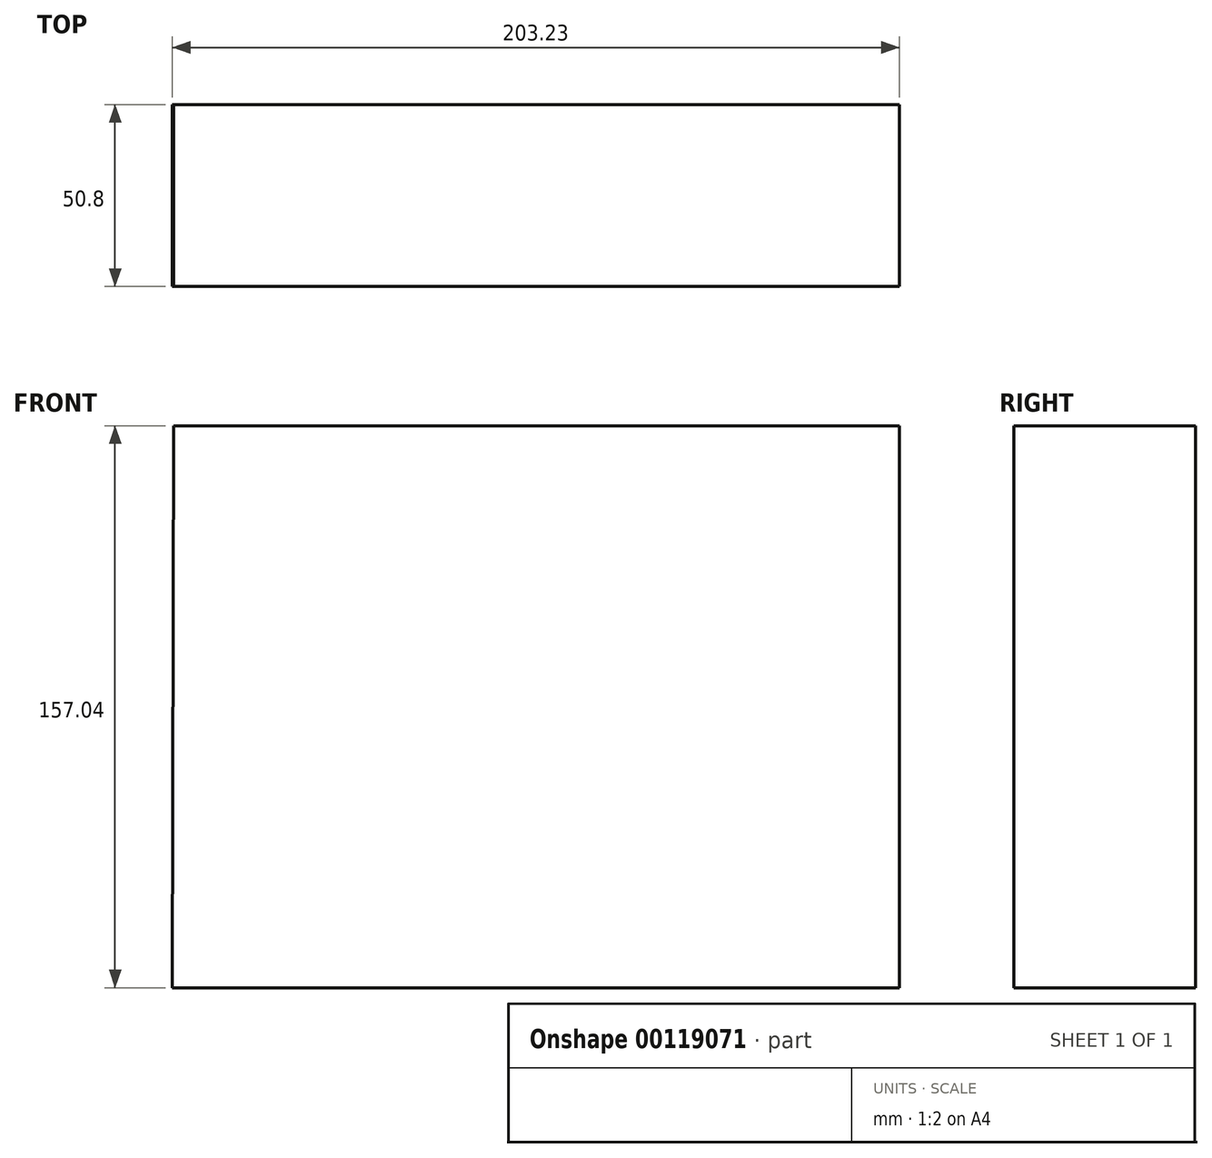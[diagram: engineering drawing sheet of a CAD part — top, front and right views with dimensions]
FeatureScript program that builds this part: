
annotation { "Feature Type Name" : "Feature", "Feature Type Description" : "" }
export const myFeature = defineFeature(function(context is Context, id is Id, definition is map)
    precondition{}
    {
        {
            var Q0;
            Q0=qCreatedBy(makeId("Front.planeOp"),FACE);
            var sketch = newSketch(context, id + "F0", { "sketchPlane" : qUnion([Q0])});
            skCircle(sketch, "E0", {"center": v(0, 0) * mm, "radius": 68.7 * mm});
            skCircle(sketch, "E1", {"center": v(0, 0) * mm, "radius": 25.42 * mm});
            skCircle(sketch, "E2", {"center": v(0, 0) * mm, "radius": 54.89 * mm});
            skLineSegment(sketch, "E3", {"start": v(-41.7, 35.68) * mm, "end": v(-19.6, 16.2) * mm});
            skLineSegment(sketch, "E4", {"start": v(-23.88, 8.7) * mm, "end": v(-46.71, 28.82) * mm});
            skLineSegment(sketch, "E5", {"start": v(-4.77, 54.68) * mm, "end": v(-4.77, 24.97) * mm});
            skLineSegment(sketch, "E6", {"start": v(5.39, 54.62) * mm, "end": v(5.39, 24.84) * mm});
            skLineSegment(sketch, "E7", {"start": v(17.58, 18.36) * mm, "end": v(38.51, 39.11) * mm});
            skLineSegment(sketch, "E8", {"start": v(38.51, 39.11) * mm, "end": v(17.58, 18.36) * mm});
            skLineSegment(sketch, "E9", {"start": v(22.8, 11.24) * mm, "end": v(44.23, 32.5) * mm});
            skLineSegment(sketch, "E10", {"start": v(24.53, -6.66) * mm, "end": v(51.45, -19.11) * mm});
            skLineSegment(sketch, "E11", {"start": v(21.26, -13.93) * mm, "end": v(48.14, -26.36) * mm});
            skLineSegment(sketch, "E12", {"start": v(6.01, -24.7) * mm, "end": v(6.01, -54.56) * mm});
            skLineSegment(sketch, "E13", {"start": v(6.01, -54.56) * mm, "end": v(6.01, -24.7) * mm});
            skLineSegment(sketch, "E14", {"start": v(-4.16, -25.08) * mm, "end": v(-4.16, -54.73) * mm});
            skLineSegment(sketch, "E15", {"start": v(-4.16, -54.73) * mm, "end": v(-4.16, -25.08) * mm});
            skLineSegment(sketch, "E16", {"start": v(-22.39, -12.04) * mm, "end": v(-48.5, -25.7) * mm});
            skLineSegment(sketch, "E17", {"start": v(-48.5, -25.7) * mm, "end": v(-22.39, -12.04) * mm});
            skLineSegment(sketch, "E18", {"start": v(-24.94, -4.9) * mm, "end": v(-51.56, -18.81) * mm});
            skCircle(sketch, "E19", {"center": v(0, 0) * mm, "radius": 21.1 * mm});
            skSolve(sketch);
        }
        {
            var Q0;
            {var subQ0=sQuery(id+"F0.wireOp",EDGE,"E3");Q0=makeQuery(id+"F0.imprint","IMPRINT",FACE,{"disambiguationData":[TD([[makeQuery(id+"F0.imprint","IMPRINT",EDGE,{"derivedFrom":subQ0}),-1.0]])]});}
            var Q1;
            {var subQ0=sQuery(id+"F0.wireOp",EDGE,"E17");Q1=makeQuery(id+"F0.imprint","IMPRINT",FACE,{"disambiguationData":[TD([[makeQuery(id+"F0.imprint","IMPRINT",EDGE,{"derivedFrom":subQ0}),1.0]])]});}
            var Q2;
            Q2=makeQuery(id+"F0.imprint","IMPRINT",FACE,{"disambiguationData":[TD([[makeQuery(id+"F0.imprint","IMPRINT",EDGE,{"derivedFrom":sQuery(id+"F0.wireOp",EDGE,"E0")}),1.0]])]});
            var Q3;
            {var subQ0=sQuery(id+"F0.wireOp",EDGE,"E13");Q3=makeQuery(id+"F0.imprint","IMPRINT",FACE,{"disambiguationData":[TD([[makeQuery(id+"F0.imprint","IMPRINT",EDGE,{"derivedFrom":subQ0}),1.0]])]});}
            var Q4;
            {var subQ0=sQuery(id+"F0.wireOp",EDGE,"E10");Q4=makeQuery(id+"F0.imprint","IMPRINT",FACE,{"disambiguationData":[TD([[makeQuery(id+"F0.imprint","IMPRINT",EDGE,{"derivedFrom":subQ0}),-1.0]])]});}
            var Q5;
            {var subQ0=sQuery(id+"F0.wireOp",EDGE,"E8");Q5=makeQuery(id+"F0.imprint","IMPRINT",FACE,{"disambiguationData":[TD([[makeQuery(id+"F0.imprint","IMPRINT",EDGE,{"derivedFrom":subQ0}),1.0]])]});}
            var Q6;
            {var subQ0=sQuery(id+"F0.wireOp",EDGE,"E5");Q6=makeQuery(id+"F0.imprint","IMPRINT",FACE,{"disambiguationData":[TD([[makeQuery(id+"F0.imprint","IMPRINT",EDGE,{"derivedFrom":subQ0}),1.0]])]});}
            var Q7;
            Q7=makeQuery(id+"F0.imprint","IMPRINT",FACE,{"disambiguationData":[TD([[makeQuery(id+"F0.imprint","IMPRINT",EDGE,{"derivedFrom":sQuery(id+"F0.wireOp",EDGE,"E19")}),-1.0]])]});
            extrude(context, id + "F1", {"entities" : qUnion([Q0, Q1, Q2, Q3, Q4, Q5, Q6, Q7]), "depth" : 25.4 * mm});
        }
        {
            var Q0;
            Q0=makeQuery(id+"F1.opExtrude","SWEPT_FACE",FACE,{"disambiguationData":[OSD([sQuery(id+"F0.wireOp",EDGE,"E0")])]});
            shell(context, id + "F2", {"entities" : qUnion([Q0]), "thickness" : 2.54 * mm});
        }
        {
            var Q0;
            Q0=qCreatedBy(makeId("Front.planeOp"),FACE);
            var sketch = newSketch(context, id + "F3", { "sketchPlane" : qUnion([Q0])});
            skLineSegment(sketch, "E20", {"start": v(-105.49, 77.63) * mm, "end": v(97.44, 77.63) * mm});
            skLineSegment(sketch, "E21", {"start": v(97.44, 77.63) * mm, "end": v(97.44, -79.41) * mm});
            skLineSegment(sketch, "E22", {"start": v(97.44, -79.41) * mm, "end": v(-105.79, -79.41) * mm});
            skLineSegment(sketch, "E23", {"start": v(-105.79, -79.41) * mm, "end": v(-105.49, 77.63) * mm});
            skSolve(sketch);
        }
        {
            var Q0;
            Q0 = qSketchRegion(id + "F3", true);
            extrude(context, id + "F4", {"entities" : qUnion([Q0]), "operationType" : NewBodyOperationType.ADD, "depth" : 50.8 * mm});
        }
    });
